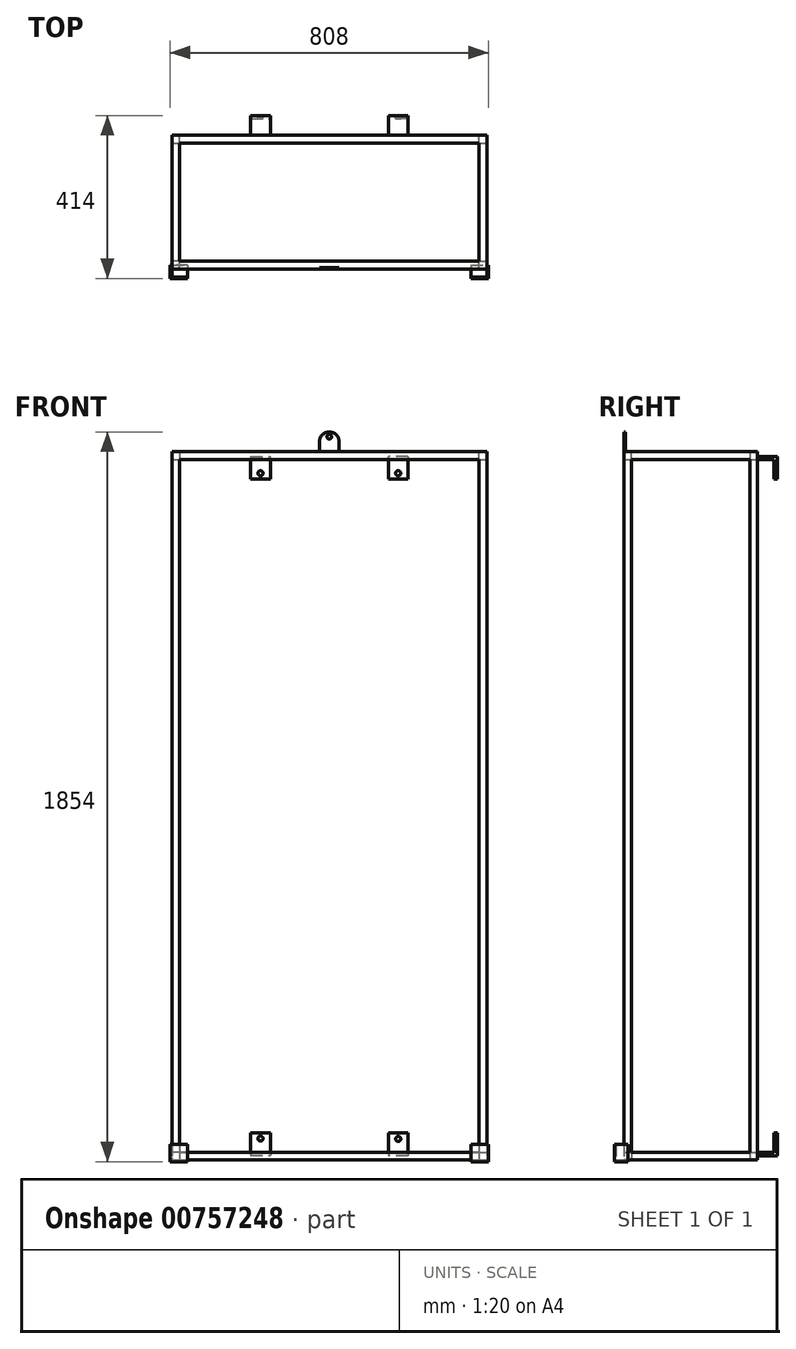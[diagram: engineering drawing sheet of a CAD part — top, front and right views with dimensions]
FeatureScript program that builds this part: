
annotation { "Feature Type Name" : "Feature", "Feature Type Description" : "" }
export const myFeature = defineFeature(function(context is Context, id is Id, definition is map)
    precondition{}
    {
        {
            var Q0;
            Q0=qCreatedBy(makeId("Front.planeOp"),FACE);
            var sketch = newSketch(context, id + "F0", { "sketchPlane" : qUnion([Q0])});
            skLineSegment(sketch, "E0.bottom", {"start": v(-37.58, 1743.9) * mm, "end": v(762.42, 1743.9) * mm});
            skLineSegment(sketch, "E0.top", {"start": v(-37.58, -56.1) * mm, "end": v(762.42, -56.1) * mm});
            skLineSegment(sketch, "E0.left", {"start": v(-37.58, 1743.9) * mm, "end": v(-37.58, -56.1) * mm});
            skLineSegment(sketch, "E0.right", {"start": v(762.42, 1743.9) * mm, "end": v(762.42, -56.1) * mm});
            skLineSegment(sketch, "E1.bottom", {"start": v(742.42, 1723.9) * mm, "end": v(-17.58, 1723.9) * mm});
            skLineSegment(sketch, "E1.top", {"start": v(742.42, -36.1) * mm, "end": v(-17.58, -36.1) * mm});
            skLineSegment(sketch, "E1.left", {"start": v(742.42, 1723.9) * mm, "end": v(742.42, -36.1) * mm});
            skLineSegment(sketch, "E1.right", {"start": v(-17.58, 1723.9) * mm, "end": v(-17.58, -36.1) * mm});
            skSolve(sketch);
        }
        {
            var Q0;
            Q0 = qSketchRegion(id + "F0", true);
            extrude(context, id + "F1", {"entities" : qUnion([Q0]), "depth" : 20 * mm, "offsetDistance" : 25 * mm});
        }
        {
            var Q0;
            Q0=makeQuery(id+"F1.opExtrude","CAP_FACE",FACE,{"disambiguationData":[OSD([sQuery(id+"F0.wireOp",EDGE,"E0.bottom"),sQuery(id+"F0.wireOp",EDGE,"E0.top"),sQuery(id+"F0.wireOp",EDGE,"E0.left"),sQuery(id+"F0.wireOp",EDGE,"E0.right"),sQuery(id+"F0.wireOp",EDGE,"E1.bottom"),sQuery(id+"F0.wireOp",EDGE,"E1.top"),sQuery(id+"F0.wireOp",EDGE,"E1.left"),sQuery(id+"F0.wireOp",EDGE,"E1.right")])],"isStart":false});
            var sketch = newSketch(context, id + "F2", { "sketchPlane" : qUnion([Q0])});
            skLineSegment(sketch, "E2.bottom", {"start": v(742.42, 1723.9) * mm, "end": v(762.42, 1723.9) * mm});
            skLineSegment(sketch, "E2.top", {"start": v(742.42, 1743.9) * mm, "end": v(762.42, 1743.9) * mm});
            skLineSegment(sketch, "E2.left", {"start": v(742.42, 1723.9) * mm, "end": v(742.42, 1743.9) * mm});
            skLineSegment(sketch, "E2.right", {"start": v(762.42, 1723.9) * mm, "end": v(762.42, 1743.9) * mm});
            skLineSegment(sketch, "E3.bottom", {"start": v(742.42, -36.1) * mm, "end": v(762.42, -36.1) * mm});
            skLineSegment(sketch, "E3.top", {"start": v(742.42, -56.1) * mm, "end": v(762.42, -56.1) * mm});
            skLineSegment(sketch, "E3.left", {"start": v(742.42, -36.1) * mm, "end": v(742.42, -56.1) * mm});
            skLineSegment(sketch, "E3.right", {"start": v(762.42, -36.1) * mm, "end": v(762.42, -56.1) * mm});
            skLineSegment(sketch, "E4.bottom", {"start": v(-17.58, -36.1) * mm, "end": v(-37.58, -36.1) * mm});
            skLineSegment(sketch, "E4.top", {"start": v(-17.58, -56.1) * mm, "end": v(-37.58, -56.1) * mm});
            skLineSegment(sketch, "E4.left", {"start": v(-17.58, -36.1) * mm, "end": v(-17.58, -56.1) * mm});
            skLineSegment(sketch, "E4.right", {"start": v(-37.58, -36.1) * mm, "end": v(-37.58, -56.1) * mm});
            skLineSegment(sketch, "E5.bottom", {"start": v(-37.58, 1743.9) * mm, "end": v(-17.58, 1743.9) * mm});
            skLineSegment(sketch, "E5.top", {"start": v(-37.58, 1723.9) * mm, "end": v(-17.58, 1723.9) * mm});
            skLineSegment(sketch, "E5.left", {"start": v(-37.58, 1743.9) * mm, "end": v(-37.58, 1723.9) * mm});
            skLineSegment(sketch, "E5.right", {"start": v(-17.58, 1743.9) * mm, "end": v(-17.58, 1723.9) * mm});
            skSolve(sketch);
        }
        {
            var Q0;
            Q0 = qSketchRegion(id + "F2", true);
            extrude(context, id + "F3", {"entities" : qUnion([Q0]), "operationType" : NewBodyOperationType.ADD, "depth" : 300 * mm, "offsetDistance" : 25 * mm});
        }
        {
            var Q0;
            Q0=makeQuery(id+"F3.opExtrude","CAP_FACE",FACE,{"disambiguationData":[OSD([sQuery(id+"F2.wireOp",EDGE,"E5.bottom"),sQuery(id+"F2.wireOp",EDGE,"E5.top"),sQuery(id+"F2.wireOp",EDGE,"E5.left"),sQuery(id+"F2.wireOp",EDGE,"E5.right")])],"isStart":false});
            var sketch = newSketch(context, id + "F4", { "sketchPlane" : qUnion([Q0])});
            skLineSegment(sketch, "E6.bottom", {"start": v(-37.58, 1743.9) * mm, "end": v(762.42, 1743.9) * mm});
            skLineSegment(sketch, "E6.top", {"start": v(-37.58, -56.1) * mm, "end": v(762.42, -56.1) * mm});
            skLineSegment(sketch, "E6.left", {"start": v(-37.58, 1743.9) * mm, "end": v(-37.58, -56.1) * mm});
            skLineSegment(sketch, "E6.right", {"start": v(762.42, 1743.9) * mm, "end": v(762.42, -56.1) * mm});
            skLineSegment(sketch, "E7.bottom", {"start": v(-17.58, 1723.9) * mm, "end": v(742.42, 1723.9) * mm});
            skLineSegment(sketch, "E7.top", {"start": v(-17.58, -36.1) * mm, "end": v(742.42, -36.1) * mm});
            skLineSegment(sketch, "E7.left", {"start": v(-17.58, 1723.9) * mm, "end": v(-17.58, -36.1) * mm});
            skLineSegment(sketch, "E7.right", {"start": v(742.42, 1723.9) * mm, "end": v(742.42, -36.1) * mm});
            skSolve(sketch);
        }
        {
            var Q0;
            Q0 = qSketchRegion(id + "F4", true);
            extrude(context, id + "F5", {"entities" : qUnion([Q0]), "operationType" : NewBodyOperationType.ADD, "depth" : 20 * mm, "offsetDistance" : 25 * mm});
        }
        {
            var Q0;
            Q0=makeQuery(id+"F1.opExtrude","CAP_FACE",FACE,{"disambiguationData":[OSD([sQuery(id+"F0.wireOp",EDGE,"E0.bottom"),sQuery(id+"F0.wireOp",EDGE,"E0.top"),sQuery(id+"F0.wireOp",EDGE,"E0.left"),sQuery(id+"F0.wireOp",EDGE,"E0.right"),sQuery(id+"F0.wireOp",EDGE,"E1.bottom"),sQuery(id+"F0.wireOp",EDGE,"E1.top"),sQuery(id+"F0.wireOp",EDGE,"E1.left"),sQuery(id+"F0.wireOp",EDGE,"E1.right")])],"isStart":true});
            var sketch = newSketch(context, id + "F6", { "sketchPlane" : qUnion([Q0])});
            skLineSegment(sketch, "E8", {"start": v(-562.42, 1731.9) * mm, "end": v(-562.42, 1723.9) * mm});
            skLineSegment(sketch, "E9", {"start": v(-162.42, 1731.9) * mm, "end": v(-162.42, 1723.9) * mm});
            skLineSegment(sketch, "E10.bottom", {"start": v(-562.42, 1723.9) * mm, "end": v(-512.42, 1723.9) * mm});
            skLineSegment(sketch, "E10.top", {"start": v(-562.42, 1731.9) * mm, "end": v(-512.42, 1731.9) * mm});
            skLineSegment(sketch, "E10.left", {"start": v(-562.42, 1723.9) * mm, "end": v(-562.42, 1731.9) * mm});
            skLineSegment(sketch, "E10.right", {"start": v(-512.42, 1723.9) * mm, "end": v(-512.42, 1731.9) * mm});
            skLineSegment(sketch, "E11.bottom", {"start": v(-162.42, 1723.9) * mm, "end": v(-212.42, 1723.9) * mm});
            skLineSegment(sketch, "E11.top", {"start": v(-162.42, 1731.9) * mm, "end": v(-212.42, 1731.9) * mm});
            skLineSegment(sketch, "E11.left", {"start": v(-162.42, 1723.9) * mm, "end": v(-162.42, 1731.9) * mm});
            skLineSegment(sketch, "E11.right", {"start": v(-212.42, 1723.9) * mm, "end": v(-212.42, 1731.9) * mm});
            skLineSegment(sketch, "E12.bottom", {"start": v(-562.42, -37.45) * mm, "end": v(-512.42, -37.45) * mm});
            skLineSegment(sketch, "E12.top", {"start": v(-562.42, -45.45) * mm, "end": v(-512.42, -45.45) * mm});
            skLineSegment(sketch, "E12.left", {"start": v(-562.42, -37.45) * mm, "end": v(-562.42, -45.45) * mm});
            skLineSegment(sketch, "E12.right", {"start": v(-512.42, -37.45) * mm, "end": v(-512.42, -45.45) * mm});
            skLineSegment(sketch, "E13.bottom", {"start": v(-162.42, -36.31) * mm, "end": v(-212.42, -36.31) * mm});
            skLineSegment(sketch, "E13.top", {"start": v(-162.42, -44.31) * mm, "end": v(-212.42, -44.31) * mm});
            skLineSegment(sketch, "E13.left", {"start": v(-162.42, -36.31) * mm, "end": v(-162.42, -44.31) * mm});
            skLineSegment(sketch, "E13.right", {"start": v(-212.42, -36.31) * mm, "end": v(-212.42, -44.31) * mm});
            skPoint(sketch, "E14.start.orphan", {"position": v(-562.42, 1689.22) * mm});
            skSolve(sketch);
        }
        {
            var Q0;
            Q0 = qSketchRegion(id + "F6", true);
            extrude(context, id + "F7", {"entities" : qUnion([Q0]), "operationType" : NewBodyOperationType.ADD, "depth" : 50 * mm, "offsetDistance" : 25 * mm});
        }
        {
            var Q0;
            Q0=makeQuery(id+"F7.boolean.opBoolean","MERGE",FACE,{"derivedFrom":[makeQuery(id+"F1.opExtrude","SWEPT_FACE",FACE,{"disambiguationData":[OSD([sQuery(id+"F0.wireOp",EDGE,"E1.bottom")])]}),makeQuery(id+"F7.opExtrude","SWEPT_FACE",FACE,{"disambiguationData":[OSD([sQuery(id+"F6.wireOp",EDGE,"E10.bottom")])]}),makeQuery(id+"F7.opExtrude","SWEPT_FACE",FACE,{"disambiguationData":[OSD([sQuery(id+"F6.wireOp",EDGE,"E11.bottom")])]})]});
            var sketch = newSketch(context, id + "F8", { "sketchPlane" : qUnion([Q0])});
            skLineSegment(sketch, "E15.bottom", {"start": v(562.42, -50) * mm, "end": v(512.42, -50) * mm});
            skLineSegment(sketch, "E15.top", {"start": v(562.42, -42) * mm, "end": v(512.42, -42) * mm});
            skLineSegment(sketch, "E15.left", {"start": v(562.42, -50) * mm, "end": v(562.42, -42) * mm});
            skLineSegment(sketch, "E15.right", {"start": v(512.42, -50) * mm, "end": v(512.42, -42) * mm});
            skLineSegment(sketch, "E16.bottom", {"start": v(212.42, -50) * mm, "end": v(162.42, -50) * mm});
            skLineSegment(sketch, "E16.top", {"start": v(212.42, -42) * mm, "end": v(162.42, -42) * mm});
            skLineSegment(sketch, "E16.left", {"start": v(212.42, -50) * mm, "end": v(212.42, -42) * mm});
            skLineSegment(sketch, "E16.right", {"start": v(162.42, -50) * mm, "end": v(162.42, -42) * mm});
            skSolve(sketch);
        }
        {
            var Q0;
            Q0 = qSketchRegion(id + "F8", true);
            extrude(context, id + "F9", {"entities" : qUnion([Q0]), "operationType" : NewBodyOperationType.ADD, "depth" : 50 * mm, "offsetDistance" : 25 * mm});
        }
        {
            var Q0;
            Q0=makeQuery(id+"F7.opExtrude","SWEPT_FACE",FACE,{"disambiguationData":[OSD([sQuery(id+"F6.wireOp",EDGE,"E13.bottom")])]});
            var sketch = newSketch(context, id + "F10", { "sketchPlane" : qUnion([Q0])});
            skLineSegment(sketch, "E17.bottom", {"start": v(162.42, 50) * mm, "end": v(212.42, 50) * mm});
            skLineSegment(sketch, "E17.top", {"start": v(162.42, 42) * mm, "end": v(212.42, 42) * mm});
            skLineSegment(sketch, "E17.left", {"start": v(162.42, 50) * mm, "end": v(162.42, 42) * mm});
            skLineSegment(sketch, "E17.right", {"start": v(212.42, 50) * mm, "end": v(212.42, 42) * mm});
            skSolve(sketch);
        }
        {
            var Q0;
            Q0 = qSketchRegion(id + "F10", true);
            extrude(context, id + "F11", {"entities" : qUnion([Q0]), "operationType" : NewBodyOperationType.ADD, "depth" : 50 * mm, "offsetDistance" : 25 * mm});
        }
        {
            var Q0;
            Q0=makeQuery(id+"F7.opExtrude","SWEPT_FACE",FACE,{"disambiguationData":[OSD([sQuery(id+"F6.wireOp",EDGE,"E12.bottom")])]});
            var sketch = newSketch(context, id + "F12", { "sketchPlane" : qUnion([Q0])});
            skLineSegment(sketch, "E18.bottom", {"start": v(512.42, 50) * mm, "end": v(562.42, 50) * mm});
            skLineSegment(sketch, "E18.top", {"start": v(512.42, 42) * mm, "end": v(562.42, 42) * mm});
            skLineSegment(sketch, "E18.left", {"start": v(512.42, 50) * mm, "end": v(512.42, 42) * mm});
            skLineSegment(sketch, "E18.right", {"start": v(562.42, 50) * mm, "end": v(562.42, 42) * mm});
            skSolve(sketch);
        }
        {
            var Q0;
            Q0 = qSketchRegion(id + "F12", true);
            extrude(context, id + "F13", {"entities" : qUnion([Q0]), "operationType" : NewBodyOperationType.ADD, "depth" : 50 * mm, "offsetDistance" : 25 * mm});
        }
        {
            var Q0;
            Q0=makeQuery(id+"F11.boolean.opBoolean","MERGE",FACE,{"derivedFrom":[makeQuery(id+"F7.opExtrude","CAP_FACE",FACE,{"disambiguationData":[OSD([sQuery(id+"F6.wireOp",EDGE,"E13.bottom"),sQuery(id+"F6.wireOp",EDGE,"E13.top"),sQuery(id+"F6.wireOp",EDGE,"E13.left"),sQuery(id+"F6.wireOp",EDGE,"E13.right")])],"isStart":false}),makeQuery(id+"F11.opExtrude","SWEPT_FACE",FACE,{"disambiguationData":[OSD([sQuery(id+"F10.wireOp",EDGE,"E17.bottom")])]})]});
            var sketch = newSketch(context, id + "F14", { "sketchPlane" : qUnion([Q0])});
            skCircle(sketch, "E19", {"center": v(-187.42, -1.31) * mm, "radius": 6.5 * mm});
            skPoint(sketch, "E20.start.orphan", {"position": v(-187.42, 13.69) * mm});
            skSolve(sketch);
        }
        {
            var Q0;
            Q0 = qSketchRegion(id + "F14", true);
            extrude(context, id + "F15", {"entities" : qUnion([Q0]), "operationType" : NewBodyOperationType.REMOVE, "oppositeDirection" : true, "depth" : 25 * mm, "offsetDistance" : 25 * mm});
        }
        {
            var Q0;
            Q0=makeQuery(id+"F13.boolean.opBoolean","MERGE",FACE,{"derivedFrom":[makeQuery(id+"F7.opExtrude","CAP_FACE",FACE,{"disambiguationData":[OSD([sQuery(id+"F6.wireOp",EDGE,"E12.bottom"),sQuery(id+"F6.wireOp",EDGE,"E12.top"),sQuery(id+"F6.wireOp",EDGE,"E12.left"),sQuery(id+"F6.wireOp",EDGE,"E12.right")])],"isStart":false}),makeQuery(id+"F13.opExtrude","SWEPT_FACE",FACE,{"disambiguationData":[OSD([sQuery(id+"F12.wireOp",EDGE,"E18.bottom")])]})]});
            var sketch = newSketch(context, id + "F16", { "sketchPlane" : qUnion([Q0])});
            skCircle(sketch, "E21", {"center": v(-537.42, -2.45) * mm, "radius": 6.5 * mm});
            skPoint(sketch, "E22.start.orphan", {"position": v(-537.42, 12.55) * mm});
            skSolve(sketch);
        }
        {
            var Q0;
            Q0 = qSketchRegion(id + "F16", true);
            extrude(context, id + "F17", {"entities" : qUnion([Q0]), "operationType" : NewBodyOperationType.REMOVE, "oppositeDirection" : true, "depth" : 25 * mm, "offsetDistance" : 25 * mm});
        }
        {
            var Q0;
            Q0=makeQuery(id+"F9.boolean.opBoolean","MERGE",FACE,{"derivedFrom":[makeQuery(id+"F7.opExtrude","CAP_FACE",FACE,{"disambiguationData":[OSD([sQuery(id+"F6.wireOp",EDGE,"E11.bottom"),sQuery(id+"F6.wireOp",EDGE,"E11.top"),sQuery(id+"F6.wireOp",EDGE,"E11.left"),sQuery(id+"F6.wireOp",EDGE,"E11.right")])],"isStart":false}),makeQuery(id+"F9.opExtrude","SWEPT_FACE",FACE,{"disambiguationData":[OSD([sQuery(id+"F8.wireOp",EDGE,"E16.bottom")])]})]});
            var sketch = newSketch(context, id + "F18", { "sketchPlane" : qUnion([Q0])});
            skCircle(sketch, "E23", {"center": v(-187.45, 1688.9) * mm, "radius": 6.5 * mm});
            skPoint(sketch, "E24.orphan", {"position": v(-187.42, 1673.9) * mm});
            skSolve(sketch);
        }
        {
            var Q0;
            Q0 = qSketchRegion(id + "F18", true);
            extrude(context, id + "F19", {"entities" : qUnion([Q0]), "operationType" : NewBodyOperationType.REMOVE, "oppositeDirection" : true, "depth" : 25 * mm, "offsetDistance" : 25 * mm});
        }
        {
            var Q0;
            Q0=makeQuery(id+"F9.boolean.opBoolean","MERGE",FACE,{"derivedFrom":[makeQuery(id+"F7.opExtrude","CAP_FACE",FACE,{"disambiguationData":[OSD([sQuery(id+"F6.wireOp",EDGE,"E10.bottom"),sQuery(id+"F6.wireOp",EDGE,"E10.top"),sQuery(id+"F6.wireOp",EDGE,"E10.left"),sQuery(id+"F6.wireOp",EDGE,"E10.right")])],"isStart":false}),makeQuery(id+"F9.opExtrude","SWEPT_FACE",FACE,{"disambiguationData":[OSD([sQuery(id+"F8.wireOp",EDGE,"E15.bottom")])]})]});
            var sketch = newSketch(context, id + "F20", { "sketchPlane" : qUnion([Q0])});
            skCircle(sketch, "E25", {"center": v(-537.42, 1688.9) * mm, "radius": 6.5 * mm});
            skPoint(sketch, "E26.orphan", {"position": v(-537.42, 1673.9) * mm});
            skSolve(sketch);
        }
        {
            var Q0;
            Q0 = qSketchRegion(id + "F20", true);
            extrude(context, id + "F21", {"entities" : qUnion([Q0]), "operationType" : NewBodyOperationType.REMOVE, "oppositeDirection" : true, "depth" : 25 * mm, "offsetDistance" : 25 * mm});
        }
        {
            var Q0;
            Q0=makeQuery(id+"F5.opExtrude","CAP_FACE",FACE,{"disambiguationData":[OSD([sQuery(id+"F4.wireOp",EDGE,"E6.bottom"),sQuery(id+"F4.wireOp",EDGE,"E6.top"),sQuery(id+"F4.wireOp",EDGE,"E6.left"),sQuery(id+"F4.wireOp",EDGE,"E6.right"),sQuery(id+"F4.wireOp",EDGE,"E7.bottom"),sQuery(id+"F4.wireOp",EDGE,"E7.top"),sQuery(id+"F4.wireOp",EDGE,"E7.left"),sQuery(id+"F4.wireOp",EDGE,"E7.right")])],"isStart":false});
            var sketch = newSketch(context, id + "F22", { "sketchPlane" : qUnion([Q0])});
            skLineSegment(sketch, "E27", {"start": v(362.42, 1743.9) * mm, "end": v(337.42, 1743.9) * mm});
            skLineSegment(sketch, "E28", {"start": v(362.42, 1743.9) * mm, "end": v(387.42, 1743.9) * mm});
            skArc(sketch, "E29", {"start": v(387.42, 1768.9) * mm, "mid": v(362.42, 1793.9) * mm, "end": v(337.42, 1768.9) * mm});
            skLineSegment(sketch, "E30", {"start": v(337.42, 1743.9) * mm, "end": v(337.42, 1768.9) * mm});
            skLineSegment(sketch, "E31", {"start": v(387.42, 1743.9) * mm, "end": v(387.42, 1768.9) * mm});
            skPoint(sketch, "E32.end.orphan", {"position": v(362.42, 1793.9) * mm});
            skCircle(sketch, "E33", {"center": v(362.42, 1781.9) * mm, "radius": 6 * mm});
            skSolve(sketch);
        }
        {
            var Q0;
            Q0 = qSketchRegion(id + "F22", true);
            extrude(context, id + "F23", {"entities" : qUnion([Q0]), "oppositeDirection" : true, "depth" : 4 * mm, "offsetDistance" : 25 * mm});
        }
        {
            var Q0;
            Q0=makeQuery(id+"F5.opExtrude","CAP_FACE",FACE,{"disambiguationData":[OSD([sQuery(id+"F4.wireOp",EDGE,"E6.bottom"),sQuery(id+"F4.wireOp",EDGE,"E6.top"),sQuery(id+"F4.wireOp",EDGE,"E6.left"),sQuery(id+"F4.wireOp",EDGE,"E6.right"),sQuery(id+"F4.wireOp",EDGE,"E7.bottom"),sQuery(id+"F4.wireOp",EDGE,"E7.top"),sQuery(id+"F4.wireOp",EDGE,"E7.left"),sQuery(id+"F4.wireOp",EDGE,"E7.right")])],"isStart":false});
            var sketch = newSketch(context, id + "F24", { "sketchPlane" : qUnion([Q0])});
            skLineSegment(sketch, "E34.bottom", {"start": v(-37.58, -56.1) * mm, "end": v(2.42, -56.1) * mm});
            skLineSegment(sketch, "E34.left", {"start": v(-37.58, -56.1) * mm, "end": v(-37.58, -16.1) * mm});
            skLineSegment(sketch, "E35", {"start": v(-37.58, -16.1) * mm, "end": v(-41.58, -16.1) * mm});
            skLineSegment(sketch, "E36", {"start": v(-41.58, -16.1) * mm, "end": v(-41.58, -60.1) * mm});
            skLineSegment(sketch, "E37", {"start": v(2.42, -56.1) * mm, "end": v(2.42, -60.1) * mm});
            skLineSegment(sketch, "E38", {"start": v(2.42, -60.1) * mm, "end": v(-41.58, -60.1) * mm});
            skSolve(sketch);
        }
        {
            var Q0;
            Q0 = qSketchRegion(id + "F24", true);
            extrude(context, id + "F25", {"entities" : qUnion([Q0]), "operationType" : NewBodyOperationType.ADD, "oppositeDirection" : true, "depth" : 10 * mm, "offsetDistance" : 25 * mm});
        }
        {
            var Q0;
            Q0 = qSketchRegion(id + "F24", true);
            extrude(context, id + "F26", {"entities" : qUnion([Q0]), "operationType" : NewBodyOperationType.ADD, "depth" : 20 * mm, "offsetDistance" : 25 * mm});
        }
        {
            var Q0;
            Q0=makeQuery(id+"F26.opExtrude","CAP_FACE",FACE,{"disambiguationData":[OSD([sQuery(id+"F24.wireOp",EDGE,"E34.bottom"),sQuery(id+"F24.wireOp",EDGE,"E34.left"),sQuery(id+"F24.wireOp",EDGE,"E35"),sQuery(id+"F24.wireOp",EDGE,"E36"),sQuery(id+"F24.wireOp",EDGE,"E37"),sQuery(id+"F24.wireOp",EDGE,"E38")])],"isStart":false});
            var sketch = newSketch(context, id + "F27", { "sketchPlane" : qUnion([Q0])});
            skLineSegment(sketch, "E39.bottom", {"start": v(-41.58, -16.1) * mm, "end": v(2.42, -16.1) * mm});
            skLineSegment(sketch, "E39.top", {"start": v(-41.58, -60.1) * mm, "end": v(2.42, -60.1) * mm});
            skLineSegment(sketch, "E39.left", {"start": v(-41.58, -16.1) * mm, "end": v(-41.58, -60.1) * mm});
            skLineSegment(sketch, "E39.right", {"start": v(2.42, -16.1) * mm, "end": v(2.42, -60.1) * mm});
            skSolve(sketch);
        }
        {
            var Q0;
            Q0 = qSketchRegion(id + "F27", true);
            extrude(context, id + "F28", {"entities" : qUnion([Q0]), "operationType" : NewBodyOperationType.ADD, "depth" : 4 * mm, "offsetDistance" : 25 * mm});
        }
        {
            var Q0;
            Q0=makeQuery(id+"F25.boolean.opBoolean","MERGE",FACE,{"derivedFrom":[makeQuery(id+"F5.opExtrude","CAP_FACE",FACE,{"disambiguationData":[OSD([sQuery(id+"F4.wireOp",EDGE,"E6.bottom"),sQuery(id+"F4.wireOp",EDGE,"E6.top"),sQuery(id+"F4.wireOp",EDGE,"E6.left"),sQuery(id+"F4.wireOp",EDGE,"E6.right"),sQuery(id+"F4.wireOp",EDGE,"E7.bottom"),sQuery(id+"F4.wireOp",EDGE,"E7.top"),sQuery(id+"F4.wireOp",EDGE,"E7.left"),sQuery(id+"F4.wireOp",EDGE,"E7.right")])],"isStart":false}),makeQuery(id+"F25.opExtrude","CAP_FACE",FACE,{"disambiguationData":[OSD([sQuery(id+"F24.wireOp",EDGE,"E34.bottom"),sQuery(id+"F24.wireOp",EDGE,"E34.left"),sQuery(id+"F24.wireOp",EDGE,"E35"),sQuery(id+"F24.wireOp",EDGE,"E36"),sQuery(id+"F24.wireOp",EDGE,"E37"),sQuery(id+"F24.wireOp",EDGE,"E38")])],"isStart":true})]});
            var sketch = newSketch(context, id + "F29", { "sketchPlane" : qUnion([Q0])});
            skLineSegment(sketch, "E40.bottom", {"start": v(762.42, -56.1) * mm, "end": v(722.42, -56.1) * mm});
            skLineSegment(sketch, "E40.left", {"start": v(762.42, -56.1) * mm, "end": v(762.42, -16.1) * mm});
            skLineSegment(sketch, "E41", {"start": v(722.42, -56.1) * mm, "end": v(722.42, -60.1) * mm});
            skLineSegment(sketch, "E42", {"start": v(762.42, -16.1) * mm, "end": v(766.42, -16.1) * mm});
            skLineSegment(sketch, "E43", {"start": v(722.42, -60.1) * mm, "end": v(766.42, -60.1) * mm});
            skLineSegment(sketch, "E44", {"start": v(766.42, -16.1) * mm, "end": v(766.42, -60.1) * mm});
            skSolve(sketch);
        }
        {
            var Q0;
            Q0 = qSketchRegion(id + "F29", true);
            extrude(context, id + "F30", {"entities" : qUnion([Q0]), "operationType" : NewBodyOperationType.ADD, "oppositeDirection" : true, "depth" : 10 * mm, "offsetDistance" : 25 * mm});
        }
        {
            var Q0;
            Q0 = qSketchRegion(id + "F29", true);
            extrude(context, id + "F31", {"entities" : qUnion([Q0]), "operationType" : NewBodyOperationType.ADD, "depth" : 20 * mm, "offsetDistance" : 25 * mm});
        }
        {
            var Q0;
            Q0=makeQuery(id+"F31.opExtrude","CAP_FACE",FACE,{"disambiguationData":[OSD([sQuery(id+"F29.wireOp",EDGE,"E40.bottom"),sQuery(id+"F29.wireOp",EDGE,"E40.left"),sQuery(id+"F29.wireOp",EDGE,"E41"),sQuery(id+"F29.wireOp",EDGE,"E42"),sQuery(id+"F29.wireOp",EDGE,"E43"),sQuery(id+"F29.wireOp",EDGE,"E44")])],"isStart":false});
            var sketch = newSketch(context, id + "F32", { "sketchPlane" : qUnion([Q0])});
            skLineSegment(sketch, "E45.bottom", {"start": v(722.42, -60.1) * mm, "end": v(766.42, -60.1) * mm});
            skLineSegment(sketch, "E45.top", {"start": v(722.42, -16.1) * mm, "end": v(766.42, -16.1) * mm});
            skLineSegment(sketch, "E45.left", {"start": v(722.42, -60.1) * mm, "end": v(722.42, -16.1) * mm});
            skLineSegment(sketch, "E45.right", {"start": v(766.42, -60.1) * mm, "end": v(766.42, -16.1) * mm});
            skSolve(sketch);
        }
        {
            var Q0;
            Q0 = qSketchRegion(id + "F32", true);
            extrude(context, id + "F33", {"entities" : qUnion([Q0]), "operationType" : NewBodyOperationType.ADD, "depth" : 4 * mm, "offsetDistance" : 25 * mm});
        }
    });
